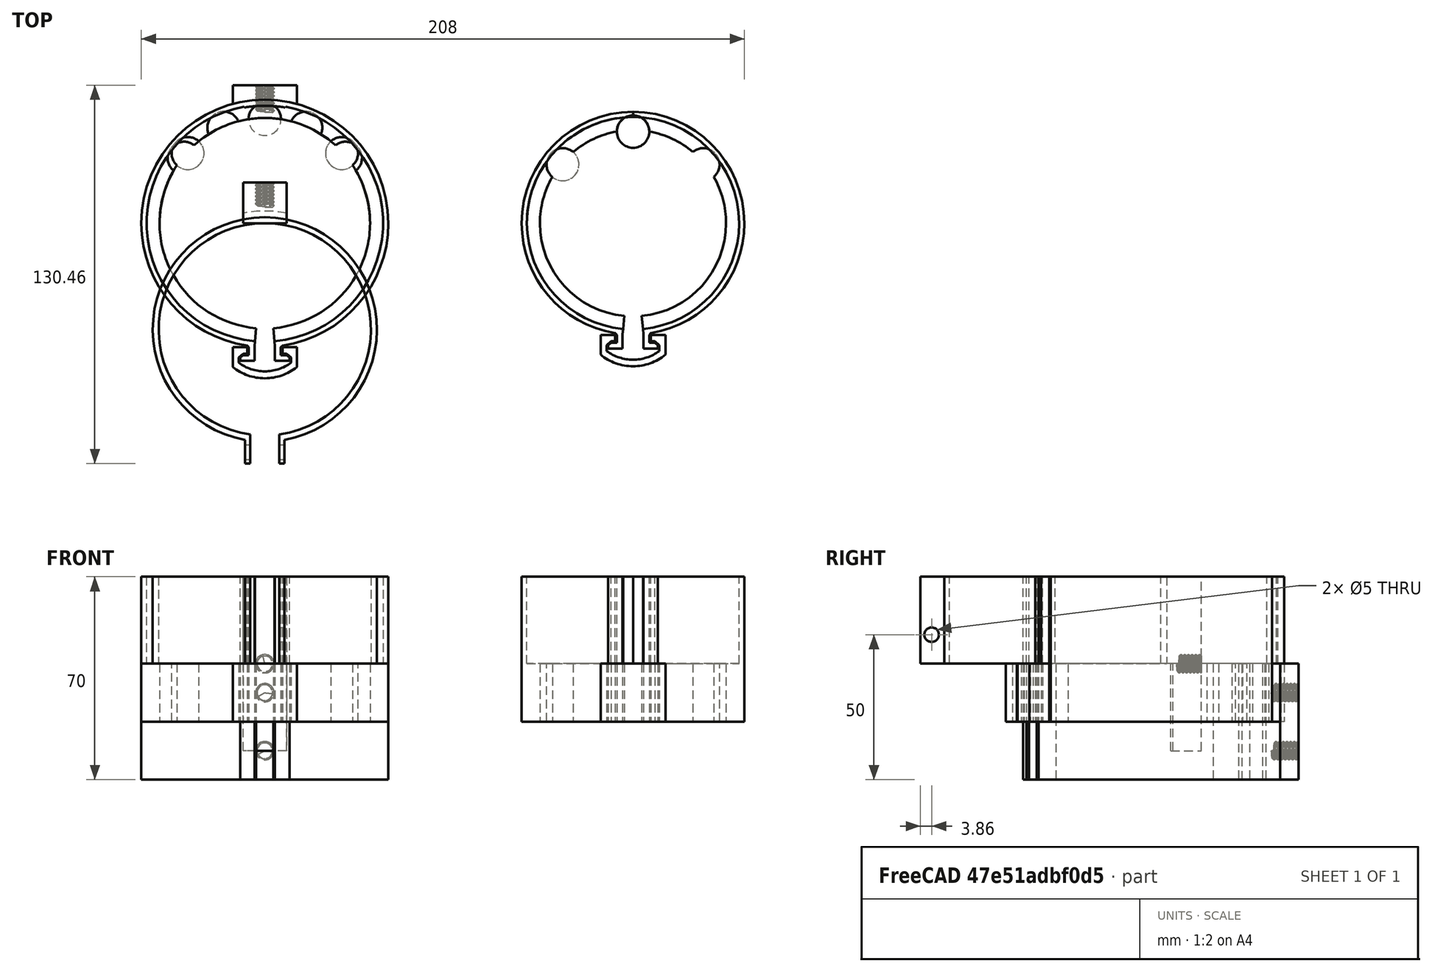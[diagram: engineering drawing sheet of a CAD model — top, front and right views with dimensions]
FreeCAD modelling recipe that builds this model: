
FCSTD DOCUMENT  (FreeCAD 0.21R33771 (Git))
Label: the-poor-mans-telescope-stabilize
License: All rights reserved
LicenseURL: http://en.wikipedia.org/wiki/All_rights_reserved
objects: Sketcher::SketchObject×25, PartDesign::Pad×21, PartDesign::Body×7, PartDesign::Mirrored×7, App::Part×3, PartDesign::SubtractiveHelix×2, PartDesign::Pocket×2, PartDesign::ShapeBinder×2, Spreadsheet::Sheet×1, PartDesign::LinearPattern×1
note: 92 computed .brp shape members not serialized (recipe doc carries the construction recipe); baked Part::Feature solids carry a one-line shape summary decoded from their .brp

FEATURE [Spreadsheet::Sheet] Spreadsheet
  cells = A1='LENS SETTINGS; D1='S; E1='M; A2='Eyepiece holder radius; B2(eyepiece_holder_radius)=30; D2=22; E2=30; A4='TWEAKING SETTINGS; A5='Thickness; B5(wall_thickness)=1.8; C5='Wall thickness; A6='Gap; B6(gap)=0.6; C6='Gap between bodies; A8='CALCULATED VALUES; A10='Inner radius; B10(radious)==eyepiece_holder_radius + wall_thickness * 3 + gap; A11='Firs tube section radius; B11(first_tube_section_radius)==eyepiece_holder_radius + wall_thickness + gap; C11='The  radius of the thinest part of the tube; A12='Second tube section radius; B12(second_tube_section_radius)==eyepiece_holder_radius + wall_thickness * 3 + gap * 2; A13='Third tube section radius; B13(third_tube_section_radius)==eyepiece_holder_radius + wall_thickness * 5 + gap * 3
FEATURE [Sketcher::SketchObject] Sketch005
  FullyConstrained = true
  MapMode = 5
  Support = -> [XY_Plane022]
  sketch-geometry (6):
    g0: LineSegment StartX=-3.175 StartY=15.535 StartZ=0 EndX=-3.175 EndY=15.735 EndZ=0
    g1: LineSegment StartX=-3.175 StartY=15.735 StartZ=0 EndX=-2.675 EndY=16.27 EndZ=0
    g2: LineSegment StartX=-2.675 StartY=16.27 StartZ=0 EndX=0 EndY=16.27 EndZ=0
    g3: LineSegment StartX=0 StartY=16.27 StartZ=0 EndX=0 EndY=15 EndZ=0
    g4: LineSegment StartX=0 StartY=15 StartZ=0 EndX=-2.675 EndY=15 EndZ=0
    g5: LineSegment StartX=-2.675 StartY=15 StartZ=0 EndX=-3.175 EndY=15.535 EndZ=0
  constraints (18):
    c: Vertical(g0)
    c: Coincident(g0,g1)
    c: Coincident(g1,g2)
    c: Horizontal(g2)
    c: Coincident(g2,g3)
    c: Vertical(g3)
    c: Coincident(g3,g4)
    c: Horizontal(g4)
    c: Coincident(g4,g5)
    c: Coincident(g5,g0)
    c: Vertical(g1,g4)
    c: DistanceY(g0,g0) = 0.2
    c: Equal(g5,g1)
    c: DistanceY(g3,g3) = 1.27
    c: DistanceX(g2,g2) = 2.675
    c: DistanceX(g0,g3) = 3.175
    c: PointOnObject(g2,g-2)
    c: DistanceY(g-1,g3) = 15
FEATURE [Sketcher::SketchObject] Sketch007
  FullyConstrained = true
  MapMode = 5
  Support = -> [XY_Plane022]
  sketch-geometry (1):
    g0: LineSegment StartX=0 StartY=3 StartZ=0 EndX=0 EndY=12 EndZ=0
  constraints (4):
    c: Vertical(g0)
    c: PointOnObject(g0,g-2)
    c: DistanceY(g-1,g0) = 12
    c: DistanceY(g-1,g0) = 3
FEATURE [Sketcher::SketchObject] Sketch008
  FullyConstrained = true
  MapMode = 5
  Placement = pos=(0,0,0) rot=(1,0,0;1.5708rad)
  Support = -> [XZ_Plane022]
  sketch-geometry (4):
    g0: LineSegment StartX=-7.5 StartY=30 StartZ=0 EndX=7.5 EndY=30 EndZ=0
    g1: LineSegment StartX=7.5 StartY=30 StartZ=0 EndX=7.5 EndY=-30 EndZ=0
    g2: LineSegment StartX=7.5 StartY=-30 StartZ=0 EndX=-7.5 EndY=-30 EndZ=0
    g3: LineSegment StartX=-7.5 StartY=-30 StartZ=0 EndX=-7.5 EndY=30 EndZ=0
  constraints (10):
    c: Coincident(g0,g1)
    c: Coincident(g1,g2)
    c: Coincident(g2,g3)
    c: Coincident(g3,g0)
    c: Horizontal(g2)
    c: Vertical(g3)
    c: DistanceX(g0,g0) = 15
    c: Symmetric(g0,g1,g-1)
    c: DistanceY(g3,g3) = 60
    c: Symmetric(g0,g0,g-2)
FEATURE [PartDesign::Pad] Pad003
  Direction = (0,-1,-2e-16)
  Length = 14
  Length2 = 10
  Placement = pos=(0,0,0) rot=(1,0,0;1.5708rad)
  Profile = -> Sketch008
  ReferenceAxis = -> Sketch008 [N_Axis]
  Reversed = true
  Type = 0
FEATURE [PartDesign::SubtractiveHelix] SubtractiveHelix
  Angle = 0
  Axis = (0,1,0)
  Base = (0,0,0)
  BaseFeature = -> Pad003
  Growth = 0
  HasBeenEdited = true
  Height = 9.5
  LeftHanded = false
  Mode = 0
  Outside = false
  Pitch = 1.27
  Placement = pos=(0,0,0) rot=(1,0,0;1.5708rad)
  Profile = -> Sketch005
  ReferenceAxis = -> Sketch005 [V_Axis]
  Reversed = true
  Turns = 7.48031
FEATURE [Sketcher::SketchObject] Sketch009
  FullyConstrained = true
  MapMode = 5
  Support = -> [XY_Plane023]
  expr: Constraints[10] = Spreadsheet.wall_thickness
  expr: Constraints[18] = Spreadsheet.wall_thickness
  expr: Constraints[20] = Spreadsheet.second_tube_section_radius
  expr: Constraints[23] = Spreadsheet.second_tube_section_radius
  sketch-geometry (8):
    g0: ArcOfCircle CenterX=-8.4e-15 CenterY=-36.6 CenterZ=0 NormalX=0 NormalY=0 NormalZ=1 AngleXU=0 Radius=38.6596 StartAngle=4.8892 EndAngle=10.8188
    g1: ArcOfCircle CenterX=-8.4e-15 CenterY=-36.6 CenterZ=0 NormalX=0 NormalY=0 NormalZ=1 AngleXU=0 Radius=36.6 StartAngle=4.84943 EndAngle=10.8585
    g2: LineSegment StartX=-6.8 StartY=-74.6569 StartZ=0 EndX=-6.8 EndY=-82.8569 EndZ=0
    g3: LineSegment StartX=-6.8 StartY=-82.8569 StartZ=0 EndX=-5 EndY=-82.8569 EndZ=0
    g4: LineSegment StartX=-5 StartY=-82.8569 StartZ=0 EndX=-5 EndY=-72.8569 EndZ=0
    g5: LineSegment StartX=6.8 StartY=-74.6569 StartZ=0 EndX=6.8 EndY=-82.8569 EndZ=0
    g6: LineSegment StartX=6.8 StartY=-82.8569 StartZ=0 EndX=5 EndY=-82.8569 EndZ=0
    g7: LineSegment StartX=5 StartY=-82.8569 StartZ=0 EndX=5 EndY=-72.8569 EndZ=0
  constraints (24):
    c: Coincident(g1,g0)
    c: Symmetric(g1,g1,g-2)
    c: Coincident(g0,g2)
    c: Coincident(g2,g3)
    c: Coincident(g3,g4)
    c: Coincident(g4,g1)
    c: Coincident(g0,g5)
    c: Coincident(g5,g6)
    c: Coincident(g6,g7)
    c: Coincident(g7,g1)
    c: DistanceX(g3,g3) = 1.8
    c: Horizontal(g3)
    c: Horizontal(g6)
    c: Vertical(g2)
    c: Vertical(g4)
    c: Vertical(g7)
    c: Vertical(g5)
    c: DistanceX(g1,g1) = 10
    c: DistanceY(g0,g1) = 1.8
    c: Equal(g3,g6)
    c: Radius(g1) = 36.6
    c: Horizontal(g3,g6)
    c: DistanceY(g4,g4) = 10
    c: DistanceY(g0,g-1) = 36.6
FEATURE [PartDesign::Pad] Pad004
  Direction = (0,0,1)
  Length = 30
  Length2 = 10
  Profile = -> Sketch009
  ReferenceAxis = -> Sketch009 [N_Axis]
  Type = 0
FEATURE [Sketcher::SketchObject] Sketch010
  FullyConstrained = true
  MapMode = 5
  Support = -> [XY_Plane022]
  expr: Constraints[3] = Spreadsheet.third_tube_section_radius
  expr: Constraints[6] = Spreadsheet.second_tube_section_radius
  sketch-geometry (2):
    g0: ArcOfCircle CenterX=0 CenterY=-36.6 CenterZ=0 NormalX=0 NormalY=0 NormalZ=1 AngleXU=0 Radius=40.8 StartAngle=1.11307 EndAngle=2.02852
    g1: LineSegment StartX=-18.03 StartY=-2.771e-13 StartZ=0 EndX=18.03 EndY=-2.771e-13 EndZ=0
  constraints (7):
    c: PointOnObject(g0,g-2)
    c: Horizontal(g0,g0)
    c: PointOnObject(g0,g-1)
    c: Radius(g0) = 40.8
    c: Coincident(g1,g0)
    c: Coincident(g1,g0)
    c: DistanceY(g0,g-1) = 36.6
FEATURE [PartDesign::Pocket] Pocket001
  BaseFeature = -> SubtractiveHelix
  Direction = (0,0,-1)
  Length = 40
  Length2 = 5
  Placement = pos=(0,0,0) rot=(1,0,0;1.5708rad)
  Profile = -> Sketch010
  ReferenceAxis = -> Sketch010 [N_Axis]
  Type = 0
FEATURE [PartDesign::Body] Body015
  Group = -> [Sketch005,Sketch007,Sketch008,Pad003,SubtractiveHelix,Sketch010,Pocket001]
  Origin = -> Origin022
  Tip = -> Pocket001
FEATURE [Sketcher::SketchObject] Sketch011
  FullyConstrained = true
  MapMode = 5
  Placement = pos=(0,0,0) rot=(0.57735,0.57735,0.57735;2.0944rad)
  Support = -> [YZ_Plane023]
  expr: Constraints[2] = Spreadsheet.second_tube_section_radius * 2 + Spreadsheet.wall_thickness + 4
  sketch-geometry (1):
    g0: Circle CenterX=-79 CenterY=10 CenterZ=0 NormalX=0 NormalY=0 NormalZ=1 AngleXU=0 Radius=2.5
  constraints (3):
    c: Radius(g0) = 2.5
    c: DistanceY(g-1,g0) = 10
    c: DistanceX(g0,g-1) = 79
FEATURE [PartDesign::Pocket] Pocket002
  BaseFeature = -> Pad004
  Direction = (-1,2e-16,-3e-16)
  Length = 5
  Length2 = 5
  Midplane = true
  Profile = -> Sketch011
  ReferenceAxis = -> Sketch011 [N_Axis]
  Type = 1
FEATURE [PartDesign::Body] Body016
  Group = -> [Sketch009,Pad004,Sketch011,Pocket002]
  Origin = -> Origin023
  Tip = -> Pocket002
FEATURE [App::Part] Part002  label="Mount connector"
  Group = -> [Body016,Body015]
  Origin = -> Origin021
  Placement = pos=(0,-79,0) rot=(0,0,1;0rad)
FEATURE [Sketcher::SketchObject] Sketch016
  FullyConstrained = true
  MapMode = 5
  Support = -> [XY_Plane026]
  expr: .Constraints.InnerTubeD = Spreadsheet.second_tube_section_radius - 0.3
  expr: .Constraints.InnerTubeD_2 = Spreadsheet.second_tube_section_radius - 0.3
  expr: .Constraints.OuterTubeOuterD = Spreadsheet.third_tube_section_radius + Spreadsheet.wall_thickness
  sketch-geometry (7):
    g0: ArcOfCircle CenterX=0 CenterY=0 CenterZ=0 NormalX=0 NormalY=0 NormalZ=1 AngleXU=0 Radius=42.6 StartAngle=1.5708 EndAngle=3.14159
    g1: ArcOfCircle CenterX=0 CenterY=0 CenterZ=0 NormalX=0 NormalY=0 NormalZ=1 AngleXU=0 Radius=36.3 StartAngle=1.72568 EndAngle=2.24928
    g2: ArcOfCircle CenterX=0 CenterY=35.8654 CenterZ=0 NormalX=0 NormalY=0 NormalZ=1 AngleXU=0 Radius=5.6 StartAngle=1.5708 EndAngle=3.14159
    g3: ArcOfCircle CenterX=-26.5478 CenterY=24.1152 CenterZ=0 NormalX=0 NormalY=0 NormalZ=1 AngleXU=0 Radius=5.6 StartAngle=0.833376 EndAngle=3.97497
    g4: ArcOfCircle CenterX=0 CenterY=0 CenterZ=0 NormalX=0 NormalY=0 NormalZ=1 AngleXU=0 Radius=36.3 StartAngle=2.55906 EndAngle=3.14159
    g5: LineSegment StartX=2.6e-15 StartY=42.6 StartZ=0 EndX=3e-16 EndY=41.4654 EndZ=0
    g6: LineSegment StartX=-42.6 StartY=5.2e-15 StartZ=0 EndX=-36.3 EndY=4.4e-15 EndZ=0
  constraints (23):
    c: Radius(g0) = 42.6  'OuterTubeOuterD'
    c: Angle(g0) = 1.5708
    c: Coincident(g2,g1)
    c: Radius(g2) = 5.6
    c: Coincident(g3,g1)
    c: Radius(g1) = 36.3  'InnerTubeD_2'
    c: PointOnObject(g2,g-2)
    c: PointOnObject(g0,g-2)
    c: Coincident(g0,g1)
    c: Coincident(g0,g-1)
    c: Radius(g3) = 5.6
    c: Angle(g3) = 3.14159
    c: Coincident(g4,g0)
    c: Coincident(g4,g3)
    c: PointOnObject(g4,g-1)
    c: Radius(g4) = 36.3  'InnerTubeD'
    c: Angle(g1) = 0.523599
    c: Angle(g2) = 1.5708
    c: Perpendicular(g2,g-2)
    c: Coincident(g5,g0)
    c: Coincident(g5,g2)
    c: Coincident(g6,g0)
    c: Coincident(g6,g4)
FEATURE [PartDesign::Pad] Pad008
  Direction = (0,0,1)
  Length = 20
  Length2 = 10
  Profile = -> Sketch016
  ReferenceAxis = -> Sketch016 [N_Axis]
  Reversed = true
  Type = 0
FEATURE [Sketcher::SketchObject] Sketch017
  ExternalGeometry = -> [Sketch016]
  FullyConstrained = true
  MapMode = 5
  Support = -> [XY_Plane026]
  expr: Constraints[9] = Spreadsheet.wall_thickness
  sketch-geometry (4):
    g0: ArcOfCircle CenterX=-6.66661e-06 CenterY=-6.66661e-06 CenterZ=0 NormalX=0 NormalY=0 NormalZ=1 AngleXU=0 Radius=40.8 StartAngle=1.5708 EndAngle=3.14159
    g1: LineSegment StartX=-40.8 StartY=8.1e-15 StartZ=0 EndX=-42.6 EndY=1.2e-15 EndZ=0
    g2: ArcOfCircle CenterX=-6.66661e-06 CenterY=-6.66661e-06 CenterZ=0 NormalX=0 NormalY=0 NormalZ=1 AngleXU=0 Radius=42.6 StartAngle=1.5708 EndAngle=3.14159
    g3: LineSegment StartX=4.9e-15 StartY=42.6 StartZ=0 EndX=2.9e-15 EndY=40.8 EndZ=0
  constraints (12):
    c: PointOnObject(g1,g-1)
    c: PointOnObject(g0,g-2)
    c: PointOnObject(g0,g-1)
    c: Coincident(g1,g0)
    c: Coincident(g2,g0)
    c: Coincident(g2,g-3)
    c: Coincident(g2,g1)
    c: Coincident(g3,g2)
    c: Coincident(g3,g0)
    c: DistanceY(g3,g3) = 1.8
    c: Angle(g0) = 1.5708
    c: Equal(g3,g1)
FEATURE [PartDesign::Pad] Pad009
  BaseFeature = -> Pad008
  Direction = (0,0,1)
  Length = 30
  Length2 = 10
  Profile = -> Sketch017
  ReferenceAxis = -> Sketch017 [N_Axis]
  Type = 0
FEATURE [Sketcher::SketchObject] Sketch018
  ExternalGeometry = -> [Sketch016]
  FullyConstrained = true
  MapMode = 5
  Support = -> [XY_Plane026]
  sketch-geometry (4):
    g0: ArcOfCircle CenterX=0 CenterY=0 CenterZ=0 NormalX=0 NormalY=0 NormalZ=1 AngleXU=0 Radius=36.3 StartAngle=3.14159 EndAngle=4.62965
    g1: ArcOfCircle CenterX=0 CenterY=0 CenterZ=0 NormalX=0 NormalY=0 NormalZ=1 AngleXU=0 Radius=42.6 StartAngle=3.14159 EndAngle=4.62965
    g2: LineSegment StartX=-3 StartY=-36.1758 StartZ=0 EndX=-3.52066 EndY=-42.4543 EndZ=0
    g3: LineSegment StartX=-42.6 StartY=5.2e-15 StartZ=0 EndX=-36.3 EndY=4.4e-15 EndZ=0
  constraints (10):
    c: Coincident(g0,g-1)
    c: Coincident(g0,g-3)
    c: Coincident(g1,g0)
    c: Coincident(g1,g-4)
    c: Coincident(g2,g0)
    c: Coincident(g2,g1)
    c: Perpendicular(g0,g2)
    c: DistanceX(g0,g-1) = 3
    c: Coincident(g3,g1)
    c: Coincident(g3,g0)
FEATURE [PartDesign::Pad] Pad010
  BaseFeature = -> Pad009
  Direction = (0,0,1)
  Length = 20
  Length2 = 10
  Profile = -> Sketch018
  ReferenceAxis = -> Sketch018 [N_Axis]
  Reversed = true
  Type = 0
FEATURE [Sketcher::SketchObject] Sketch019
  ExternalGeometry = -> [Sketch017,Sketch018,Sketch016]
  FullyConstrained = true
  MapMode = 5
  Support = -> [XY_Plane026]
  sketch-geometry (4):
    g0: ArcOfCircle CenterX=0 CenterY=0 CenterZ=0 NormalX=0 NormalY=0 NormalZ=1 AngleXU=0 Radius=42.6 StartAngle=1.5708 EndAngle=4.62965
    g1: ArcOfCircle CenterX=0 CenterY=0 CenterZ=0 NormalX=0 NormalY=0 NormalZ=1 AngleXU=0 Radius=40.8 StartAngle=1.5708 EndAngle=4.62965
    g2: LineSegment StartX=-3.3719 StartY=-40.6604 StartZ=0 EndX=-3.52066 EndY=-42.4543 EndZ=0
    g3: LineSegment StartX=2.6e-15 StartY=42.6 StartZ=0 EndX=2.5e-15 EndY=40.8 EndZ=0
  constraints (10):
    c: Coincident(g0,g-1)
    c: Coincident(g0,g-6)
    c: Coincident(g1,g0)
    c: Coincident(g1,g-7)
    c: Coincident(g2,g1)
    c: Coincident(g2,g0)
    c: Coincident(g3,g0)
    c: Coincident(g3,g1)
    c: DistanceX(g0,g-5) = 0
    c: Perpendicular(g1,g2)
FEATURE [PartDesign::Pad] Pad011
  BaseFeature = -> Pad010
  Direction = (0,0,1)
  Length = 30
  Length2 = 10
  Profile = -> Sketch019
  ReferenceAxis = -> Sketch019 [N_Axis]
  Type = 0
FEATURE [PartDesign::Mirrored] Mirrored001
  BaseFeature = -> Pad011
  MirrorPlane = -> Sketch019 [V_Axis]
  Originals = -> [Pad011,Pad010,Pad009,Pad008]
FEATURE [Sketcher::SketchObject] Sketch020
  ExternalGeometry = -> [Sketch018]
  FullyConstrained = true
  MapMode = 5
  Support = -> [XY_Plane026]
  sketch-geometry (8):
    g0: ArcOfCircle CenterX=0 CenterY=0 CenterZ=0 NormalX=0 NormalY=0 NormalZ=1 AngleXU=0 Radius=42.6 StartAngle=4.56821 EndAngle=4.62965
    g1: LineSegment StartX=-3.52066 StartY=-42.4543 StartZ=0 EndX=-3.52066 EndY=-47.4543 EndZ=0
    g2: LineSegment StartX=-3.52066 StartY=-47.4543 StartZ=0 EndX=-8.52066 EndY=-47.4543 EndZ=0
    g3: LineSegment StartX=-8.52066 StartY=-47.4543 StartZ=0 EndX=-8.52066 EndY=-46.2934 EndZ=0
    g4: LineSegment StartX=-8.52066 StartY=-46.2934 StartZ=0 EndX=-7.52066 EndY=-45.4543 EndZ=0
    g5: LineSegment StartX=-7.52066 StartY=-45.4543 StartZ=0 EndX=-5.52066 EndY=-45.4543 EndZ=0
    g6: LineSegment StartX=-5.52066 StartY=-45.4543 StartZ=0 EndX=-5.52066 EndY=-42.758 EndZ=0
    g7: LineSegment StartX=-5.52066 StartY=-42.758 StartZ=0 EndX=-6.12066 EndY=-42.158 EndZ=0
  constraints (23):
    c: Coincident(g0,g-1)
    c: Coincident(g1,g0)
    c: Vertical(g1)
    c: Coincident(g2,g1)
    c: Horizontal(g2)
    c: DistanceX(g2,g2) = 5
    c: Coincident(g2,g3)
    c: Vertical(g3)
    c: Coincident(g3,g4)
    c: Coincident(g4,g5)
    c: Horizontal(g5)
    c: Coincident(g0,g-3)
    c: DistanceY(g2,g4) = 2
    c: Angle(g3,g4) = 2.26893
    c: DistanceY(g1,g1) = 5
    c: DistanceX(g5,g5) = 2
    c: DistanceX(g5,g0) = 2
    c: Coincident(g5,g6)
    c: Vertical(g6)
    c: DistanceY(g6,g0) = 0.6
    c: Coincident(g7,g6)
    c: Coincident(g7,g0)
    c: DistanceX(g0,g6) = 0.6
FEATURE [PartDesign::Pad] Pad012
  BaseFeature = -> Mirrored001
  Direction = (0,0,1)
  Length = 30
  Length2 = 10
  Profile = -> Sketch020
  ReferenceAxis = -> Sketch020 [N_Axis]
  Type = 0
FEATURE [PartDesign::Pad] Pad013
  BaseFeature = -> Pad012
  Direction = (0,0,1)
  Length = 20
  Length2 = 10
  Profile = -> Sketch020
  ReferenceAxis = -> Sketch020 [N_Axis]
  Reversed = true
  Type = 0
FEATURE [PartDesign::Mirrored] Mirrored002
  BaseFeature = -> Pad013
  MirrorPlane = -> Sketch020 [V_Axis]
  Originals = -> [Pad012,Pad013]
FEATURE [Sketcher::SketchObject] Sketch022
  ExternalGeometry = -> [Sketch017]
  FullyConstrained = true
  MapMode = 5
  Support = -> [XY_Plane026]
  sketch-geometry (6):
    g0: ArcOfCircle CenterX=0 CenterY=0 CenterZ=0 NormalX=0 NormalY=0 NormalZ=1 AngleXU=0 Radius=40.8 StartAngle=1.5708 EndAngle=1.74533
    g1: ArcOfCircle CenterX=0 CenterY=0 CenterZ=0 NormalX=0 NormalY=0 NormalZ=1 AngleXU=0 Radius=40.4954 StartAngle=1.5708 EndAngle=1.74533
    g2: LineSegment StartX=-7.08485 StartY=40.1802 StartZ=0 EndX=-7.03195 EndY=39.8802 EndZ=0
    g3: ArcOfCircle CenterX=0 CenterY=0 CenterZ=0 NormalX=0 NormalY=0 NormalZ=1 AngleXU=0 Radius=40.8 StartAngle=1.39626 EndAngle=1.5708
    g4: ArcOfCircle CenterX=0 CenterY=0 CenterZ=0 NormalX=0 NormalY=0 NormalZ=1 AngleXU=0 Radius=40.4954 StartAngle=1.39626 EndAngle=1.5708
    g5: LineSegment StartX=7.08485 StartY=40.1802 StartZ=0 EndX=7.03195 EndY=39.8802 EndZ=0
  constraints (17):
    c: Coincident(g0,g-1)
    c: Coincident(g0,g-3)
    c: Coincident(g1,g0)
    c: PointOnObject(g1,g-2)
    c: Coincident(g2,g0)
    c: Coincident(g2,g1)
    c: Perpendicular(g1,g2)
    c: Angle(g1) = 0.174533
    c: Coincident(g3,g0)
    c: Coincident(g3,g0)
    c: Coincident(g4,g0)
    c: Coincident(g4,g1)
    c: Coincident(g5,g3)
    c: Coincident(g5,g4)
    c: Perpendicular(g4,g5)
    c: DistanceY(g1,g0) = 0.3
    c: Angle(g4) = 0.174533
FEATURE [PartDesign::Pad] Pad014
  BaseFeature = -> Mirrored002
  Direction = (0,0,1)
  Length = 30
  Length2 = 10
  Profile = -> Sketch022
  ReferenceAxis = -> Sketch022 [N_Axis]
  Type = 0
FEATURE [PartDesign::Body] Body019
  Group = -> [Sketch016,Pad008,Sketch017,Pad009,Sketch018,Pad010,Sketch019,Pad011,Mirrored001,Sketch020,Pad012,Pad013,Mirrored002,Sketch022,Pad014]
  Origin = -> Origin026
  Tip = -> Pad014
FEATURE [Sketcher::SketchObject] Sketch024
  FullyConstrained = true
  MapMode = 5
  Support = -> [XY_Plane028]
  expr: .Constraints.InnerTubeD = Spreadsheet.first_tube_section_radius - 0.3
  expr: .Constraints.InnerTubeD_2 = Spreadsheet.first_tube_section_radius - 0.3
  expr: .Constraints.OuterTubeOuterD = Spreadsheet.second_tube_section_radius + Spreadsheet.wall_thickness
  sketch-geometry (7):
    g0: ArcOfCircle CenterX=0 CenterY=0 CenterZ=0 NormalX=0 NormalY=0 NormalZ=1 AngleXU=0 Radius=38.4 StartAngle=1.5708 EndAngle=3.14159
    g1: ArcOfCircle CenterX=0 CenterY=0 CenterZ=0 NormalX=0 NormalY=0 NormalZ=1 AngleXU=0 Radius=32.1 StartAngle=1.74615 EndAngle=2.26975
    g2: ArcOfCircle CenterX=0 CenterY=31.6078 CenterZ=0 NormalX=0 NormalY=0 NormalZ=1 AngleXU=0 Radius=5.6 StartAngle=1.5708 EndAngle=3.14159
    g3: ArcOfCircle CenterX=-24.2462 CenterY=20.2774 CenterZ=0 NormalX=0 NormalY=0 NormalZ=1 AngleXU=0 Radius=5.6 StartAngle=0.874303 EndAngle=4.0159
    g4: ArcOfCircle CenterX=0 CenterY=0 CenterZ=0 NormalX=0 NormalY=0 NormalZ=1 AngleXU=0 Radius=32.1 StartAngle=2.62045 EndAngle=3.14159
    g5: LineSegment StartX=2.4e-15 StartY=38.4 StartZ=0 EndX=3e-16 EndY=37.2078 EndZ=0
    g6: LineSegment StartX=-38.4 StartY=4.7e-15 StartZ=0 EndX=-32.1 EndY=3.9e-15 EndZ=0
  constraints (23):
    c: Radius(g0) = 38.4  'OuterTubeOuterD'
    c: Angle(g0) = 1.5708
    c: Coincident(g2,g1)
    c: Radius(g2) = 5.6
    c: Coincident(g3,g1)
    c: Radius(g1) = 32.1  'InnerTubeD_2'
    c: PointOnObject(g2,g-2)
    c: PointOnObject(g0,g-2)
    c: Coincident(g0,g1)
    c: Coincident(g0,g-1)
    c: Radius(g3) = 5.6
    c: Angle(g3) = 3.14159
    c: Coincident(g4,g0)
    c: Coincident(g4,g3)
    c: PointOnObject(g4,g-1)
    c: Radius(g4) = 32.1  'InnerTubeD'
    c: Angle(g1) = 0.523599
    c: Angle(g2) = 1.5708
    c: Perpendicular(g2,g-2)
    c: Coincident(g5,g0)
    c: Coincident(g5,g2)
    c: Coincident(g6,g0)
    c: Coincident(g6,g4)
FEATURE [PartDesign::Pad] Pad015
  Direction = (0,0,1)
  Length = 20
  Length2 = 10
  Profile = -> Sketch024
  ReferenceAxis = -> Sketch024 [N_Axis]
  Reversed = true
  Type = 0
FEATURE [Sketcher::SketchObject] Sketch025
  ExternalGeometry = -> [Sketch024]
  FullyConstrained = true
  MapMode = 5
  Support = -> [XY_Plane028]
  sketch-geometry (4):
    g0: ArcOfCircle CenterX=-9.0358e-06 CenterY=9.0358e-06 CenterZ=0 NormalX=0 NormalY=0 NormalZ=1 AngleXU=0 Radius=36.6 StartAngle=1.5708 EndAngle=3.14159
    g1: LineSegment StartX=-36.6 StartY=2.2346e-12 StartZ=0 EndX=-38.4 EndY=2.1394e-12 EndZ=0
    g2: ArcOfCircle CenterX=-9.0358e-06 CenterY=9.0358e-06 CenterZ=0 NormalX=0 NormalY=0 NormalZ=1 AngleXU=0 Radius=38.4 StartAngle=1.5708 EndAngle=3.14159
    g3: LineSegment StartX=-2.1222e-12 StartY=38.4 StartZ=0 EndX=-1.80716e-05 EndY=36.6 EndZ=0
  constraints (11):
    c: PointOnObject(g0,g-1)
    c: Coincident(g1,g0)
    c: Coincident(g2,g0)
    c: Coincident(g2,g-3)
    c: Coincident(g2,g1)
    c: Coincident(g3,g2)
    c: Coincident(g3,g0)
    c: Angle(g0) = 1.5708
    c: Equal(g3,g1)
    c: DistanceY(g3,g3) = 1.8
    c: Coincident(g1,g-4)
FEATURE [PartDesign::Pad] Pad016
  BaseFeature = -> Pad015
  Direction = (0,0,1)
  Length = 30
  Length2 = 10
  Profile = -> Sketch025
  ReferenceAxis = -> Sketch025 [N_Axis]
  Type = 0
FEATURE [Sketcher::SketchObject] Sketch026
  ExternalGeometry = -> [Sketch024]
  FullyConstrained = true
  MapMode = 5
  Support = -> [XY_Plane028]
  sketch-geometry (4):
    g0: ArcOfCircle CenterX=0 CenterY=0 CenterZ=0 NormalX=0 NormalY=0 NormalZ=1 AngleXU=0 Radius=32.1 StartAngle=3.14159 EndAngle=4.61879
    g1: ArcOfCircle CenterX=0 CenterY=0 CenterZ=0 NormalX=0 NormalY=0 NormalZ=1 AngleXU=0 Radius=38.4 StartAngle=3.14159 EndAngle=4.61879
    g2: LineSegment StartX=-3 StartY=-31.9595 StartZ=0 EndX=-3.58879 EndY=-38.2319 EndZ=0
    g3: LineSegment StartX=-38.4 StartY=4.7e-15 StartZ=0 EndX=-32.1 EndY=3.9e-15 EndZ=0
  constraints (10):
    c: Coincident(g0,g-1)
    c: Coincident(g0,g-3)
    c: Coincident(g1,g0)
    c: Coincident(g1,g-4)
    c: Coincident(g2,g0)
    c: Coincident(g2,g1)
    c: Perpendicular(g0,g2)
    c: DistanceX(g0,g-1) = 3
    c: Coincident(g3,g1)
    c: Coincident(g3,g0)
FEATURE [PartDesign::Pad] Pad017
  BaseFeature = -> Pad016
  Direction = (0,0,1)
  Length = 20
  Length2 = 10
  Profile = -> Sketch026
  ReferenceAxis = -> Sketch026 [N_Axis]
  Reversed = true
  Type = 0
FEATURE [Sketcher::SketchObject] Sketch027
  ExternalGeometry = -> [Sketch025,Sketch026,Sketch024]
  FullyConstrained = true
  MapMode = 5
  Support = -> [XY_Plane028]
  sketch-geometry (4):
    g0: ArcOfCircle CenterX=0 CenterY=0 CenterZ=0 NormalX=0 NormalY=0 NormalZ=1 AngleXU=0 Radius=38.4 StartAngle=1.5708 EndAngle=4.61879
    g1: ArcOfCircle CenterX=0 CenterY=0 CenterZ=0 NormalX=0 NormalY=0 NormalZ=1 AngleXU=0 Radius=36.6 StartAngle=1.5708 EndAngle=4.61879
    g2: LineSegment StartX=-3.42056 StartY=-36.4398 StartZ=0 EndX=-3.58879 EndY=-38.2319 EndZ=0
    g3: LineSegment StartX=2.4e-15 StartY=38.4 StartZ=0 EndX=-1.80716e-05 EndY=36.6 EndZ=0
  constraints (10):
    c: Coincident(g0,g-1)
    c: Coincident(g0,g-6)
    c: Coincident(g1,g0)
    c: Coincident(g1,g-7)
    c: Coincident(g2,g1)
    c: Coincident(g2,g0)
    c: Coincident(g3,g0)
    c: Coincident(g3,g1)
    c: DistanceX(g0,g-5) = 0
    c: Perpendicular(g1,g2)
FEATURE [PartDesign::Pad] Pad018
  BaseFeature = -> Pad017
  Direction = (0,0,1)
  Length = 30
  Length2 = 10
  Profile = -> Sketch027
  ReferenceAxis = -> Sketch027 [N_Axis]
  Type = 0
FEATURE [PartDesign::Mirrored] Mirrored003
  BaseFeature = -> Pad018
  MirrorPlane = -> Sketch027 [V_Axis]
  Originals = -> [Pad018,Pad017,Pad016,Pad015]
FEATURE [Sketcher::SketchObject] Sketch028
  ExternalGeometry = -> [Sketch026]
  FullyConstrained = true
  MapMode = 5
  Support = -> [XY_Plane028]
  sketch-geometry (8):
    g0: ArcOfCircle CenterX=0 CenterY=0 CenterZ=0 NormalX=0 NormalY=0 NormalZ=1 AngleXU=0 Radius=38.4 StartAngle=4.55052 EndAngle=4.61879
    g1: LineSegment StartX=-3.58879 StartY=-38.2319 StartZ=0 EndX=-3.58879 EndY=-43.2319 EndZ=0
    g2: LineSegment StartX=-3.58879 StartY=-43.2319 StartZ=0 EndX=-8.58879 EndY=-43.2319 EndZ=0
    g3: LineSegment StartX=-8.58879 StartY=-43.2319 StartZ=0 EndX=-8.58879 EndY=-42.071 EndZ=0
    g4: LineSegment StartX=-8.58879 StartY=-42.071 StartZ=0 EndX=-7.58879 EndY=-41.2319 EndZ=0
    g5: LineSegment StartX=-7.58879 StartY=-41.2319 StartZ=0 EndX=-5.58879 EndY=-41.2319 EndZ=0
    g6: LineSegment StartX=-5.58879 StartY=-41.2319 StartZ=0 EndX=-5.58879 EndY=-38.498 EndZ=0
    g7: LineSegment StartX=-5.58879 StartY=-38.498 StartZ=0 EndX=-6.18879 EndY=-37.898 EndZ=0
  constraints (23):
    c: Coincident(g0,g-1)
    c: Coincident(g1,g0)
    c: Vertical(g1)
    c: Coincident(g2,g1)
    c: Horizontal(g2)
    c: DistanceX(g2,g2) = 5
    c: Coincident(g2,g3)
    c: Vertical(g3)
    c: Coincident(g3,g4)
    c: Coincident(g4,g5)
    c: Horizontal(g5)
    c: Coincident(g0,g-3)
    c: DistanceY(g2,g4) = 2
    c: Angle(g3,g4) = 2.26893
    c: DistanceY(g1,g1) = 5
    c: DistanceX(g5,g5) = 2
    c: DistanceX(g5,g0) = 2
    c: Coincident(g5,g6)
    c: Vertical(g6)
    c: DistanceY(g6,g0) = 0.6
    c: Coincident(g7,g6)
    c: Coincident(g7,g0)
    c: DistanceX(g0,g6) = 0.6
FEATURE [PartDesign::Pad] Pad019
  BaseFeature = -> Mirrored003
  Direction = (0,0,1)
  Length = 30
  Length2 = 10
  Profile = -> Sketch028
  ReferenceAxis = -> Sketch028 [N_Axis]
  Type = 0
FEATURE [PartDesign::Pad] Pad020
  BaseFeature = -> Pad019
  Direction = (0,0,1)
  Length = 20
  Length2 = 10
  Profile = -> Sketch028
  ReferenceAxis = -> Sketch028 [N_Axis]
  Reversed = true
  Type = 0
FEATURE [PartDesign::Mirrored] Mirrored004
  BaseFeature = -> Pad020
  MirrorPlane = -> Sketch028 [V_Axis]
  Originals = -> [Pad019,Pad020]
FEATURE [Sketcher::SketchObject] Sketch029
  ExternalGeometry = -> [Sketch025]
  FullyConstrained = true
  MapMode = 5
  Support = -> [XY_Plane028]
  sketch-geometry (6):
    g0: ArcOfCircle CenterX=0 CenterY=0 CenterZ=0 NormalX=0 NormalY=0 NormalZ=1 AngleXU=0 Radius=36.6 StartAngle=1.5708 EndAngle=1.74533
    g1: ArcOfCircle CenterX=0 CenterY=0 CenterZ=0 NormalX=0 NormalY=0 NormalZ=1 AngleXU=0 Radius=36.2954 StartAngle=1.5708 EndAngle=1.74533
    g2: LineSegment StartX=-6.35552 StartY=36.044 StartZ=0 EndX=-6.30263 EndY=35.744 EndZ=0
    g3: ArcOfCircle CenterX=0 CenterY=0 CenterZ=0 NormalX=0 NormalY=0 NormalZ=1 AngleXU=0 Radius=36.6 StartAngle=1.39626 EndAngle=1.5708
    g4: ArcOfCircle CenterX=0 CenterY=0 CenterZ=0 NormalX=0 NormalY=0 NormalZ=1 AngleXU=0 Radius=36.2954 StartAngle=1.39626 EndAngle=1.5708
    g5: LineSegment StartX=6.35552 StartY=36.044 StartZ=0 EndX=6.30263 EndY=35.744 EndZ=0
  constraints (17):
    c: Coincident(g0,g-1)
    c: Coincident(g0,g-3)
    c: Coincident(g1,g0)
    c: PointOnObject(g1,g-2)
    c: Coincident(g2,g0)
    c: Coincident(g2,g1)
    c: Perpendicular(g1,g2)
    c: Angle(g1) = 0.174533
    c: Coincident(g3,g0)
    c: Coincident(g3,g0)
    c: Coincident(g4,g0)
    c: Coincident(g4,g1)
    c: Coincident(g5,g3)
    c: Coincident(g5,g4)
    c: Perpendicular(g4,g5)
    c: DistanceY(g1,g0) = 0.3
    c: Angle(g4) = 0.174533
FEATURE [PartDesign::Body] Body020
  Group = -> [Sketch024,Pad015,Sketch025,Pad016,Sketch026,Pad017,Sketch027,Pad018,Mirrored003,Sketch028,Pad019,Pad020,Mirrored004,Sketch029]
  Origin = -> Origin028
  Placement = pos=(127,0,0) rot=(0,0,1;0rad)
  Tip = -> Mirrored004
FEATURE [PartDesign::ShapeBinder] ShapeBinder
  TraceSupport = false
FEATURE [Sketcher::SketchObject] Sketch030
  ExternalGeometry = -> [ShapeBinder]
  FullyConstrained = false
  MapMode = 5
  Support = -> [XY_Plane]
  sketch-geometry (9):
    g0: LineSegment StartX=-6.18879 StartY=-38.498 StartZ=0 EndX=-6.18879 EndY=-40.7319 EndZ=0
    g1: LineSegment StartX=-6.18879 StartY=-40.7319 StartZ=0 EndX=-7.58879 EndY=-40.7319 EndZ=0
    g2: LineSegment StartX=-7.58879 StartY=-40.7319 StartZ=0 EndX=-9.08879 EndY=-42.071 EndZ=0
    g3: LineSegment StartX=-9.08879 StartY=-42.071 StartZ=0 EndX=-9.08879 EndY=-44.071 EndZ=0
    g4: LineSegment StartX=-6.18879 StartY=-38.498 StartZ=0 EndX=-11.1888 EndY=-38.498 EndZ=0
    g5: LineSegment StartX=-11.1888 StartY=-38.498 StartZ=0 EndX=-11.1888 EndY=-45.298 EndZ=0
    g6: ArcOfCircle CenterX=0 CenterY=-31.698 CenterZ=0 NormalX=0 NormalY=0 NormalZ=1 AngleXU=0 Radius=15.3525 StartAngle=4.07884 EndAngle=4.71239
    g7: ArcOfCircle CenterX=0 CenterY=-31.698 CenterZ=0 NormalX=0 NormalY=0 NormalZ=1 AngleXU=0 Radius=17.611 StartAngle=4.02396 EndAngle=4.71239
    g8: LineSegment StartX=-2.8e-15 StartY=-47.0505 StartZ=0 EndX=-3.2e-15 EndY=-49.3091 EndZ=0
  constraints (22):
    c: Vertical(g0)
    c: Coincident(g0,g1)
    c: Coincident(g1,g2)
    c: Coincident(g2,g3)
    c: Coincident(g0,g4)
    c: Horizontal(g4)
    c: Coincident(g4,g5)
    c: Vertical(g5)
    c: PointOnObject(g6,g-2)
    c: Coincident(g6,g3)
    c: PointOnObject(g6,g-2)
    c: Coincident(g7,g6)
    c: Coincident(g7,g5)
    c: PointOnObject(g7,g-2)
    c: Coincident(g8,g6)
    c: Coincident(g8,g7)
    c: Horizontal(g1)
    c: Vertical(g3)
    c: DistanceY(g3,g3) = 2
    c: DistanceY(g5,g5) = 6.8
    c: DistanceY(g0,g6) = 6.8
    c: DistanceX(g4,g4) = 5
FEATURE [PartDesign::ShapeBinder] ShapeBinder003
  Support = -> [Pad014]
  TraceSupport = false
FEATURE [Sketcher::SketchObject] Sketch021
  ExternalGeometry = -> [ShapeBinder003]
  FullyConstrained = true
  MapMode = 5
  Support = -> [XY_Plane027]
  sketch-geometry (9):
    g0: LineSegment StartX=-6.12066 StartY=-42.758 StartZ=0 EndX=-6.12066 EndY=-44.9543 EndZ=0
    g1: LineSegment StartX=-6.12066 StartY=-44.9543 StartZ=0 EndX=-7.52066 EndY=-44.9543 EndZ=0
    g2: LineSegment StartX=-7.52066 StartY=-44.9543 StartZ=0 EndX=-9.02066 EndY=-46.2934 EndZ=0
    g3: LineSegment StartX=-9.02066 StartY=-46.2934 StartZ=0 EndX=-9.02066 EndY=-48.0934 EndZ=0
    g4: LineSegment StartX=-6.12066 StartY=-42.758 StartZ=0 EndX=-11.0207 EndY=-42.758 EndZ=0
    g5: LineSegment StartX=-11.0207 StartY=-42.758 StartZ=0 EndX=-11.0207 EndY=-49.558 EndZ=0
    g6: ArcOfCircle CenterX=0 CenterY=-35.958 CenterZ=0 NormalX=0 NormalY=0 NormalZ=1 AngleXU=0 Radius=15.1208 StartAngle=4.07317 EndAngle=4.71239
    g7: ArcOfCircle CenterX=0 CenterY=-35.958 CenterZ=0 NormalX=0 NormalY=0 NormalZ=1 AngleXU=0 Radius=17.5047 StartAngle=4.03137 EndAngle=4.71239
    g8: LineSegment StartX=-2.8e-15 StartY=-51.0788 StartZ=0 EndX=-3.2e-15 EndY=-53.4627 EndZ=0
  constraints (28):
    c: Vertical(g0)
    c: Coincident(g0,g1)
    c: Horizontal(g1)
    c: Coincident(g1,g2)
    c: Coincident(g2,g3)
    c: Vertical(g3)
    c: Coincident(g4,g0)
    c: Horizontal(g4)
    c: Coincident(g5,g4)
    c: Vertical(g5)
    c: DistanceX(g5,g3) = 2
    c: PointOnObject(g6,g-2)
    c: Coincident(g6,g3)
    c: PointOnObject(g6,g-2)
    c: Coincident(g7,g6)
    c: Coincident(g7,g5)
    c: PointOnObject(g7,g-2)
    c: Coincident(g8,g6)
    c: Coincident(g8,g7)
    c: DistanceY(g5,g5) = 6.8
    c: DistanceY(g0,g6) = 6.8
    c: DistanceX(g4,g4) = 4.9
    c: Vertical(g-3,g0)
    c: Horizontal(g0,g-4)
    c: DistanceY(g-5,g0) = 0.5
    c: Vertical(g-6,g1)
    c: Horizontal(g-7,g2)
    c: DistanceY(g3,g3) = 1.8
FEATURE [PartDesign::Pad] Pad
  Direction = (0,0,1)
  Length = 20
  Length2 = 10
  Profile = -> Sketch021
  ReferenceAxis = -> Sketch021 [N_Axis]
  Reversed = true
  Type = 0
FEATURE [PartDesign::Mirrored] Mirrored
  BaseFeature = -> Pad
  MirrorPlane = -> Sketch021 [V_Axis]
  Originals = -> [Pad]
FEATURE [PartDesign::Body] Body
  Group = -> [ShapeBinder003,Sketch021,Pad,Mirrored]
  Origin = -> Origin027
  Tip = -> Mirrored
FEATURE [PartDesign::Pad] Pad022
  Direction = (0,0,1)
  Length = 20
  Length2 = 10
  Profile = -> Sketch030
  ReferenceAxis = -> Sketch030 [N_Axis]
  Reversed = true
  Type = 0
FEATURE [PartDesign::Mirrored] Mirrored005
  BaseFeature = -> Pad022
  MirrorPlane = -> Sketch030 [V_Axis]
  Originals = -> [Pad022]
FEATURE [PartDesign::Body] Body021
  Group = -> [ShapeBinder,Sketch030,Pad022,Mirrored005]
  Origin = -> Origin
  Placement = pos=(127,0,0) rot=(0,0,1;0rad)
  Tip = -> Mirrored005
FEATURE [App::Part] Part  label="larger ring"
  Group = -> [Body019,Body]
  Origin = -> Origin029
FEATURE [App::Part] Part003  label="smaller ring"
  Group = -> [Body020,Body021]
  Origin = -> Origin030
FEATURE [Sketcher::SketchObject] Sketch031
  FullyConstrained = true
  MapMode = 5
  Support = -> [XY_Plane031]
  expr: .Constraints.InnerTubeD = Spreadsheet.second_tube_section_radius - 0.3
  expr: .Constraints.InnerTubeD_2 = Spreadsheet.second_tube_section_radius - 0.3
  expr: .Constraints.OuterTubeOuterD = Spreadsheet.third_tube_section_radius + Spreadsheet.wall_thickness
  expr: Constraints[22] = Spreadsheet.second_tube_section_radius - 0.3
  sketch-geometry (8):
    g0: ArcOfCircle CenterX=0 CenterY=0 CenterZ=0 NormalX=0 NormalY=0 NormalZ=1 AngleXU=0 Radius=42.6 StartAngle=1.5708 EndAngle=3.14159
    g1: ArcOfCircle CenterX=0 CenterY=0 CenterZ=0 NormalX=0 NormalY=0 NormalZ=1 AngleXU=0 Radius=36.3 StartAngle=2.13368 EndAngle=2.30822
    g2: ArcOfCircle CenterX=-27.9221 CenterY=22.5097 CenterZ=0 NormalX=0 NormalY=0 NormalZ=1 AngleXU=0 Radius=5.6 StartAngle=0.892309 EndAngle=4.0339
    g3: ArcOfCircle CenterX=0 CenterY=0 CenterZ=0 NormalX=0 NormalY=0 NormalZ=1 AngleXU=0 Radius=36.3 StartAngle=2.61799 EndAngle=3.14159
    g4: LineSegment StartX=-42.6 StartY=5.2e-15 StartZ=0 EndX=-36.3 EndY=4.4e-15 EndZ=0
    g5: ArcOfCircle CenterX=-14.2305 CenterY=32.9215 CenterZ=0 NormalX=0 NormalY=0 NormalZ=1 AngleXU=0 Radius=5.6 StartAngle=0.407999 EndAngle=3.54959
    g6: ArcOfCircle CenterX=0 CenterY=0 CenterZ=0 NormalX=0 NormalY=0 NormalZ=1 AngleXU=0 Radius=36.3 StartAngle=1.5708 EndAngle=1.82391
    g7: LineSegment StartX=2.6e-15 StartY=42.6 StartZ=0 EndX=2.2e-15 EndY=36.3 EndZ=0
  constraints (26):
    c: Radius(g0) = 42.6  'OuterTubeOuterD'
    c: Angle(g0) = 1.5708
    c: Coincident(g2,g1)
    c: Radius(g1) = 36.3  'InnerTubeD_2'
    c: PointOnObject(g0,g-2)
    c: Coincident(g0,g1)
    c: Coincident(g0,g-1)
    c: Radius(g2) = 5.6
    c: Angle(g2) = 3.14159
    c: Coincident(g3,g0)
    c: Coincident(g3,g2)
    c: PointOnObject(g3,g-1)
    c: Radius(g3) = 36.3  'InnerTubeD'
    c: Angle(g1) = 0.174533
    c: Coincident(g4,g0)
    c: Coincident(g4,g3)
    c: Coincident(g5,g1)
    c: Radius(g5) = 5.6
    c: Angle(g3) = 0.523599
    c: Coincident(g6,g0)
    c: Coincident(g6,g5)
    c: PointOnObject(g6,g-2)
    c: Radius(g6) = 36.3
    c: Angle(g5) = 3.14159
    c: Coincident(g7,g0)
    c: Coincident(g7,g6)
FEATURE [PartDesign::Pad] Pad023
  Direction = (0,0,1)
  Length = 40
  Length2 = 10
  Profile = -> Sketch031
  ReferenceAxis = -> Sketch031 [N_Axis]
  Reversed = true
  Type = 0
FEATURE [Sketcher::SketchObject] Sketch033
  ExternalGeometry = -> [Sketch031]
  FullyConstrained = true
  MapMode = 5
  Support = -> [XY_Plane031]
  sketch-geometry (4):
    g0: ArcOfCircle CenterX=0 CenterY=0 CenterZ=0 NormalX=0 NormalY=0 NormalZ=1 AngleXU=0 Radius=36.3 StartAngle=3.14159 EndAngle=4.62965
    g1: ArcOfCircle CenterX=0 CenterY=0 CenterZ=0 NormalX=0 NormalY=0 NormalZ=1 AngleXU=0 Radius=42.6 StartAngle=3.14159 EndAngle=4.62965
    g2: LineSegment StartX=-3 StartY=-36.1758 StartZ=0 EndX=-3.52066 EndY=-42.4543 EndZ=0
    g3: LineSegment StartX=-42.6 StartY=5.2e-15 StartZ=0 EndX=-36.3 EndY=4.4e-15 EndZ=0
  constraints (10):
    c: Coincident(g0,g-1)
    c: Coincident(g0,g-3)
    c: Coincident(g1,g0)
    c: Coincident(g1,g-4)
    c: Coincident(g2,g0)
    c: Coincident(g2,g1)
    c: DistanceX(g0,g-1) = 3
    c: Perpendicular(g0,g2)
    c: Coincident(g3,g1)
    c: Coincident(g3,g0)
FEATURE [Sketcher::SketchObject] Sketch035
  ExternalGeometry = -> [Sketch033]
  FullyConstrained = true
  MapMode = 5
  Support = -> [XY_Plane031]
  sketch-geometry (8):
    g0: ArcOfCircle CenterX=0 CenterY=0 CenterZ=0 NormalX=0 NormalY=0 NormalZ=1 AngleXU=0 Radius=42.6 StartAngle=4.56821 EndAngle=4.62965
    g1: LineSegment StartX=-3.52066 StartY=-42.4543 StartZ=0 EndX=-3.52066 EndY=-47.4543 EndZ=0
    g2: LineSegment StartX=-3.52066 StartY=-47.4543 StartZ=0 EndX=-8.52066 EndY=-47.4543 EndZ=0
    g3: LineSegment StartX=-8.52066 StartY=-47.4543 StartZ=0 EndX=-8.52066 EndY=-46.2934 EndZ=0
    g4: LineSegment StartX=-8.52066 StartY=-46.2934 StartZ=0 EndX=-7.52066 EndY=-45.4543 EndZ=0
    g5: LineSegment StartX=-7.52066 StartY=-45.4543 StartZ=0 EndX=-5.52066 EndY=-45.4543 EndZ=0
    g6: LineSegment StartX=-5.52066 StartY=-45.4543 StartZ=0 EndX=-5.52066 EndY=-42.758 EndZ=0
    g7: LineSegment StartX=-5.52066 StartY=-42.758 StartZ=0 EndX=-6.12066 EndY=-42.158 EndZ=0
  constraints (23):
    c: Coincident(g0,g-1)
    c: Coincident(g1,g0)
    c: Vertical(g1)
    c: Coincident(g2,g1)
    c: Horizontal(g2)
    c: DistanceX(g2,g2) = 5
    c: Coincident(g2,g3)
    c: Vertical(g3)
    c: Coincident(g3,g4)
    c: Coincident(g4,g5)
    c: Horizontal(g5)
    c: DistanceY(g2,g4) = 2
    c: Angle(g3,g4) = 2.26893
    c: DistanceY(g1,g1) = 5
    c: DistanceX(g5,g5) = 2
    c: DistanceX(g5,g0) = 2
    c: Coincident(g5,g6)
    c: Vertical(g6)
    c: DistanceY(g6,g0) = 0.6
    c: Coincident(g7,g6)
    c: Coincident(g7,g0)
    c: DistanceX(g0,g6) = 0.6
    c: Coincident(g0,g-4)
FEATURE [PartDesign::Pad] Pad024
  BaseFeature = -> Pad023
  Direction = (0,0,1)
  Length = 40
  Length2 = 10
  Profile = -> Sketch033
  ReferenceAxis = -> Sketch033 [N_Axis]
  Reversed = true
  Type = 0
FEATURE [PartDesign::Pad] Pad025
  BaseFeature = -> Pad024
  Direction = (0,0,1)
  Length = 40
  Length2 = 10
  Profile = -> Sketch035
  ReferenceAxis = -> Sketch035 [N_Axis]
  Reversed = true
  Type = 0
FEATURE [Sketcher::SketchObject] Sketch
  ExternalGeometry = -> [Sketch031]
  FullyConstrained = true
  MapMode = 5
  Support = -> [XY_Plane031]
  sketch-geometry (4):
    g0: ArcOfCircle CenterX=0 CenterY=0 CenterZ=0 NormalX=0 NormalY=0 NormalZ=1 AngleXU=0 Radius=42.6 StartAngle=1.5708 EndAngle=1.8326
    g1: LineSegment StartX=-11.0257 StartY=41.1484 StartZ=0 EndX=-11.0257 EndY=47.6 EndZ=0
    g2: LineSegment StartX=2.6e-15 StartY=42.6 StartZ=0 EndX=0 EndY=47.6 EndZ=0
    g3: LineSegment StartX=-11.0257 StartY=47.6 StartZ=0 EndX=0 EndY=47.6 EndZ=0
  constraints (11):
    c: Coincident(g0,g-1)
    c: Coincident(g0,g-3)
    c: Angle(g0) = 0.261799
    c: Coincident(g1,g0)
    c: Vertical(g1)
    c: Coincident(g2,g0)
    c: PointOnObject(g2,g-2)
    c: Coincident(g3,g1)
    c: Coincident(g3,g2)
    c: Horizontal(g3)
    c: DistanceY(g2,g2) = 5
FEATURE [PartDesign::Pad] Pad026
  BaseFeature = -> Pad025
  Direction = (0,0,1)
  Length = 40
  Length2 = 10
  Profile = -> Sketch
  ReferenceAxis = -> Sketch [N_Axis]
  Reversed = true
  Type = 0
FEATURE [PartDesign::Mirrored] Mirrored006
  BaseFeature = -> Pad026
  MirrorPlane = -> Sketch [V_Axis]
  Originals = -> [Pad026,Pad025,Pad024,Pad023]
FEATURE [Sketcher::SketchObject] Sketch036
  AttachmentOffset = pos=(0,0,-10) rot=(0,0,1;0rad)
  ExternalGeometry = -> [Sketch]
  FullyConstrained = true
  MapMode = 5
  Placement = pos=(0,0,-10) rot=(0,0,1;0rad)
  Support = -> [XY_Plane031]
  sketch-geometry (6):
    g0: LineSegment StartX=-2.675 StartY=48.97 StartZ=0 EndX=-3.17 EndY=48.435 EndZ=0
    g1: LineSegment StartX=-3.17 StartY=48.435 StartZ=0 EndX=-3.17 EndY=48.235 EndZ=0
    g2: LineSegment StartX=-3.17 StartY=48.235 StartZ=0 EndX=-2.675 EndY=47.7 EndZ=0
    g3: LineSegment StartX=-2.675 StartY=48.97 StartZ=0 EndX=0 EndY=48.97 EndZ=0
    g4: LineSegment StartX=-2.675 StartY=47.7 StartZ=0 EndX=0 EndY=47.7 EndZ=0
    g5: LineSegment StartX=0 StartY=47.7 StartZ=0 EndX=0 EndY=48.97 EndZ=0
  constraints (18):
    c: Coincident(g0,g1)
    c: Coincident(g1,g2)
    c: Coincident(g3,g0)
    c: DistanceX(g3,g3) = 2.675
    c: Horizontal(g3)
    c: PointOnObject(g3,g-2)
    c: DistanceX(g0,g-1) = 3.17
    c: DistanceY(g1,g1) = 0.2
    c: DistanceY(g2,g0) = 1.27
    c: Vertical(g1)
    c: Vertical(g2,g0)
    c: Coincident(g4,g2)
    c: PointOnObject(g4,g-2)
    c: Horizontal(g4)
    c: Coincident(g5,g4)
    c: Coincident(g5,g3)
    c: DistanceY(g-3,g4) = 0.1
    c: Equal(g0,g2)
FEATURE [PartDesign::SubtractiveHelix] SubtractiveHelix001
  Angle = 0
  Axis = (0,1,0)
  Base = (0,0,-10)
  BaseFeature = -> Mirrored006
  Growth = 0
  HasBeenEdited = true
  Height = 9.5
  LeftHanded = false
  Mode = 0
  Outside = false
  Pitch = 1.27
  Profile = -> Sketch036
  ReferenceAxis = -> Sketch036 [V_Axis]
  Reversed = true
  Turns = 7.48031
FEATURE [PartDesign::LinearPattern] LinearPattern
  BaseFeature = -> SubtractiveHelix001
  Direction = -> Z_Axis031
  Length = 20
  Occurrences = 2
  Originals = -> [SubtractiveHelix001]
  Reversed = true
FEATURE [PartDesign::Body] Body022
  Group = -> [Sketch031,Pad023,Sketch033,Sketch035,Pad024,Pad025,Sketch,Pad026,Mirrored006,Sketch036,SubtractiveHelix001,LinearPattern]
  Origin = -> Origin031
  Tip = -> LinearPattern
